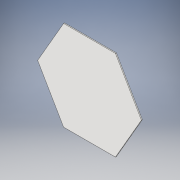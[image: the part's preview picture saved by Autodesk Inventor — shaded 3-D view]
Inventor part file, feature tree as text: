
AUTODESK INVENTOR PART (.ipt)
format: ipt  version: 2019 (Build 230136000, 136)  size: 93,696 bytes
history: native  units: mm
features: extrude x1, sketch x1
ambient origin geometry x8: Origin, YZ Plane, XZ Plane, XY Plane, X Axis, Y Axis, Z Axis, Center Point
bodies: Solid1 (feature_tree)
feature tree (2):
  extrude  "Extrusion1"  Depth=2.0mm TaperAngle=0.0deg
  sketch  "Sketch1"  dims[d0=190.0mm d1=2.0mm d2=0.0mm]
